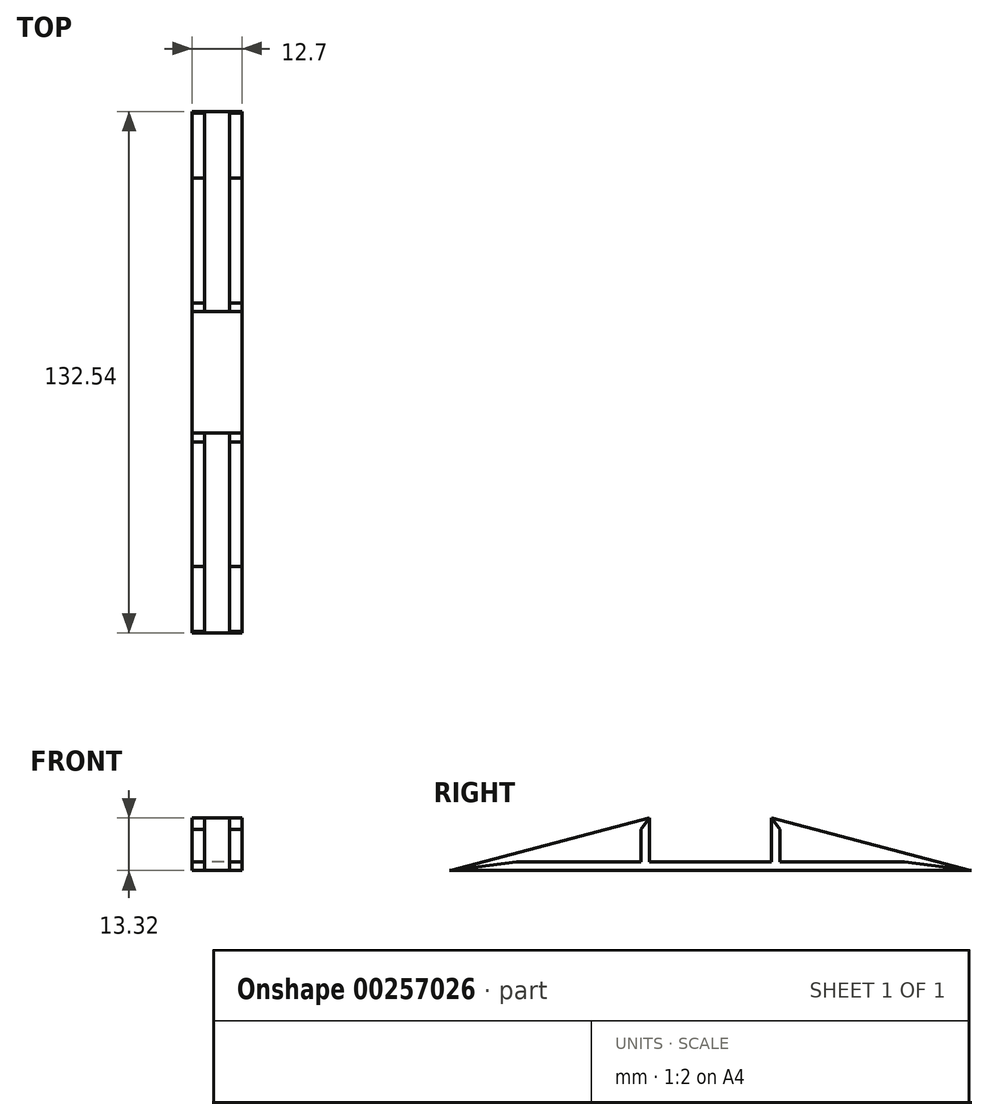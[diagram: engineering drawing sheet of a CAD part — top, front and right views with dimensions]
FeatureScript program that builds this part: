
annotation { "Feature Type Name" : "Feature", "Feature Type Description" : "" }
export const myFeature = defineFeature(function(context is Context, id is Id, definition is map)
    precondition{}
    {
        {
            var Q0;
            Q0=qCreatedBy(makeId("Right.planeOp"),FACE);
            var sketch = newSketch(context, id + "F0", { "sketchPlane" : qUnion([Q0])});
            skLineSegment(sketch, "E0.bottom", {"start": v(0, 0) * mm, "end": v(30.94, 0) * mm});
            skLineSegment(sketch, "E0.top", {"start": v(0, 13.32) * mm, "end": v(30.94, 13.32) * mm});
            skLineSegment(sketch, "E0.left", {"start": v(0, 0) * mm, "end": v(0, 13.32) * mm});
            skLineSegment(sketch, "E0.right", {"start": v(30.94, 0) * mm, "end": v(30.94, 13.32) * mm});
            skLineSegment(sketch, "E1", {"start": v(0, 0) * mm, "end": v(-50.8, 0) * mm});
            skLineSegment(sketch, "E2", {"start": v(30.94, 0) * mm, "end": v(81.74, 0) * mm});
            skLineSegment(sketch, "E3", {"start": v(30.94, 13.32) * mm, "end": v(81.74, 0) * mm});
            skLineSegment(sketch, "E4", {"start": v(-50.8, 0) * mm, "end": v(0, 13.32) * mm});
            skLineSegment(sketch, "E5.0", {"start": v(-33.85, 2.18) * mm, "end": v(-2.18, 10.49) * mm});
            skLineSegment(sketch, "E5.1", {"start": v(-2.18, 2.18) * mm, "end": v(-33.85, 2.18) * mm});
            skLineSegment(sketch, "E5.2", {"start": v(-2.18, 2.18) * mm, "end": v(-2.18, 10.49) * mm});
            skLineSegment(sketch, "E6", {"start": v(-51.2, 0) * mm, "end": v(-33.85, 2.18) * mm});
            skLineSegment(sketch, "E7", {"start": v(-2.18, 10.49) * mm, "end": v(0, 13.32) * mm});
            skLineSegment(sketch, "E8", {"start": v(15.47, 0) * mm, "end": v(15.47, 13.32) * mm, "construction": true});
            skLineSegment(sketch, "E9.MirrorCS", {"start": v(-10.21, 8.38) * mm, "end": v(-2.18, 10.49) * mm});
            skLineSegment(sketch, "E10.MirrorCS", {"start": v(33.12, 10.49) * mm, "end": v(30.94, 13.32) * mm});
            skLineSegment(sketch, "E11.MirrorCS", {"start": v(41.15, 8.38) * mm, "end": v(33.12, 10.49) * mm});
            skLineSegment(sketch, "E12.MirrorCS", {"start": v(33.12, 2.18) * mm, "end": v(33.12, 10.49) * mm});
            skLineSegment(sketch, "E13.MirrorCS", {"start": v(64.79, 2.18) * mm, "end": v(33.12, 10.49) * mm});
            skLineSegment(sketch, "E14.MirrorCS", {"start": v(82.13, 0) * mm, "end": v(64.79, 2.18) * mm});
            skLineSegment(sketch, "E15.MirrorCS", {"start": v(33.12, 2.18) * mm, "end": v(64.79, 2.18) * mm});
            skLineSegment(sketch, "E16", {"start": v(-2.18, 2.18) * mm, "end": v(0, 2.18) * mm});
            skLineSegment(sketch, "E17", {"start": v(33.12, 2.18) * mm, "end": v(-2.18, 2.18) * mm});
            skSolve(sketch);
        }
        {
            var Q0;
            {var subQ1=sQuery(id+"F0.wireOp",EDGE,"E1");Q0=makeQuery(id+"F0.imprint","IMPRINT",FACE,{"disambiguationData":[TD([[makeQuery(id+"F0.imprint","IMPRINT",EDGE,{"derivedFrom":subQ1}),-1.0]])]});}
            var Q1;
            {var subQ0=sQuery(id+"F0.wireOp",EDGE,"E0.bottom");Q1=makeQuery(id+"F0.imprint","IMPRINT",FACE,{"disambiguationData":[TD([[makeQuery(id+"F0.imprint","IMPRINT",EDGE,{"derivedFrom":subQ0}),1.0]])]});}
            var Q2;
            {var subQ4=sQuery(id+"F0.wireOp",EDGE,"E2");Q2=makeQuery(id+"F0.imprint","IMPRINT",FACE,{"disambiguationData":[TD([[makeQuery(id+"F0.imprint","IMPRINT",EDGE,{"derivedFrom":subQ4}),1.0]])]});}
            var Q3;
            {var subQ0=sQuery(id+"F0.wireOp",EDGE,"E10.MirrorCS");Q3=makeQuery(id+"F0.imprint","IMPRINT",FACE,{"disambiguationData":[TD([[makeQuery(id+"F0.imprint","IMPRINT",EDGE,{"derivedFrom":subQ0}),1.0]])]});}
            var Q4;
            {var subQ4=sQuery(id+"F0.wireOp",EDGE,"E5.2");Q4=makeQuery(id+"F0.imprint","IMPRINT",FACE,{"disambiguationData":[TD([[makeQuery(id+"F0.imprint","IMPRINT",EDGE,{"derivedFrom":subQ4}),-1.0]])]});}
            extrude(context, id + "F1", {"entities" : qUnion([Q0, Q1, Q2, Q3, Q4]), "depth" : 6.35 * mm, "offsetDistance" : 25.4 * mm, "hasSecondDirection" : true, "secondDirectionOppositeDirection" : true, "secondDirectionDepth" : 6.35 * mm});
        }
        {
            var Q0;
            {var subQ1=sQuery(id+"F0.wireOp",EDGE,"E5.0");Q0=makeQuery(id+"F0.imprint","IMPRINT",FACE,{"disambiguationData":[TD([[makeQuery(id+"F0.imprint","IMPRINT",EDGE,{"derivedFrom":subQ1}),1.0]])]});}
            var Q1;
            {var subQ1=sQuery(id+"F0.wireOp",EDGE,"E10.MirrorCS");Q1=makeQuery(id+"F0.imprint","IMPRINT",FACE,{"disambiguationData":[TD([[makeQuery(id+"F0.imprint","IMPRINT",EDGE,{"derivedFrom":subQ1}),-1.0]])]});}
            var Q2;
            {var subQ0=sQuery(id+"F0.wireOp",EDGE,"E12.MirrorCS");Q2=makeQuery(id+"F0.imprint","IMPRINT",FACE,{"disambiguationData":[TD([[makeQuery(id+"F0.imprint","IMPRINT",EDGE,{"derivedFrom":subQ0}),-1.0]])]});}
            var Q3;
            Q3=makeQuery(id+"F0.imprint","IMPRINT",FACE,{"disambiguationData":[TD([[makeQuery(id+"F0.imprint","IMPRINT",EDGE,{"derivedFrom":sQuery(id+"F0.wireOp",EDGE,"E5.0")}),-1.0]])]});
            extrude(context, id + "F2", {"entities" : qUnion([Q0, Q1, Q2, Q3]), "operationType" : NewBodyOperationType.ADD, "depth" : 3.17 * mm, "offsetDistance" : 25.4 * mm, "hasSecondDirection" : true, "secondDirectionOppositeDirection" : true, "secondDirectionDepth" : 3.17 * mm});
        }
    });
